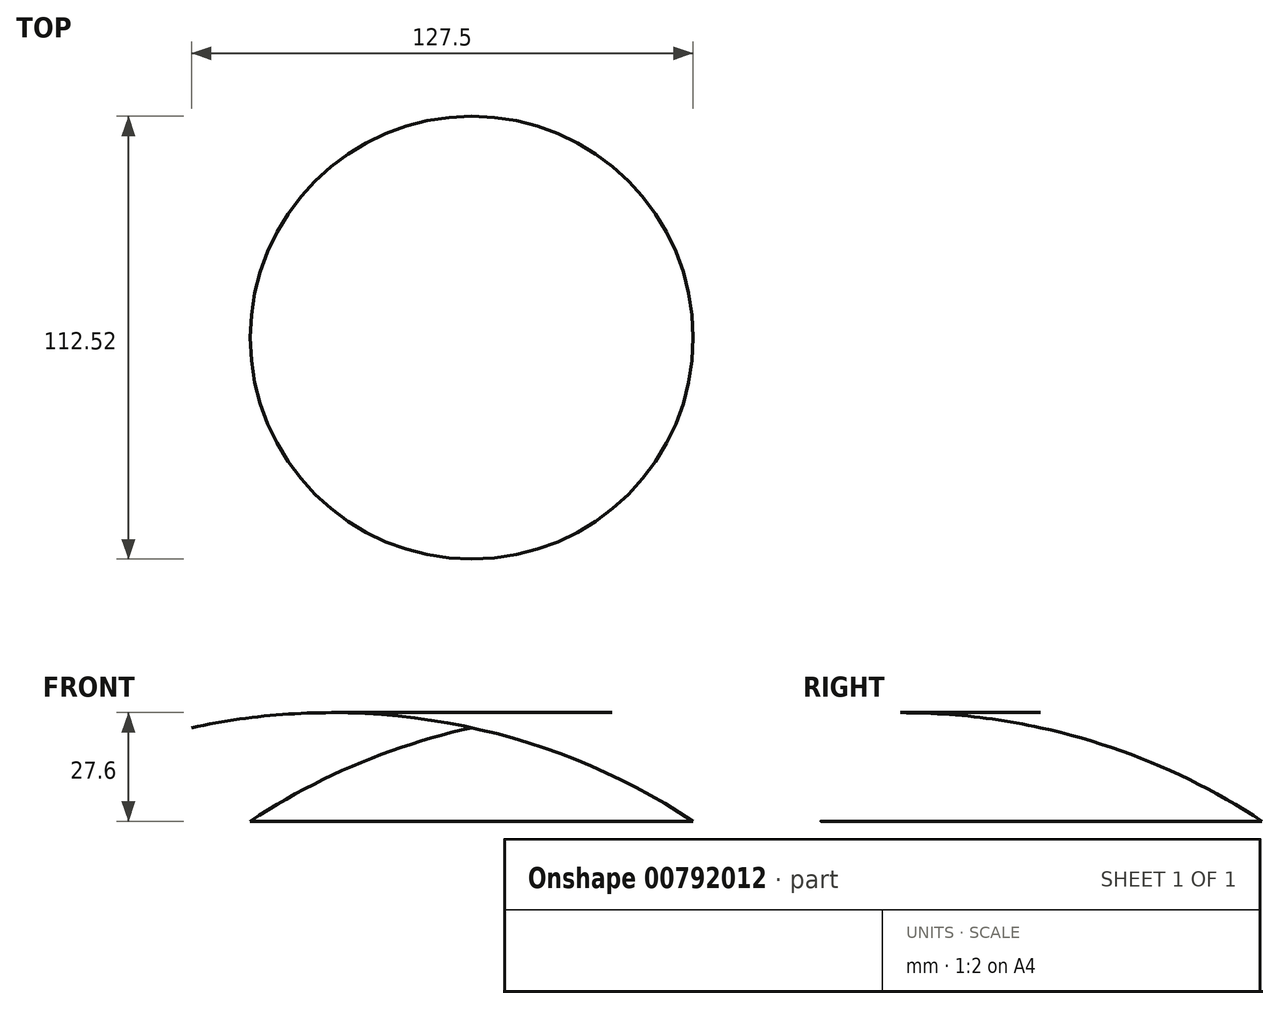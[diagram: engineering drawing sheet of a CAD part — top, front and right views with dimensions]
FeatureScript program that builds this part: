
annotation { "Feature Type Name" : "Feature", "Feature Type Description" : "" }
export const myFeature = defineFeature(function(context is Context, id is Id, definition is map)
    precondition{}
    {
        {
            var Q0;
            Q0=qCreatedBy(makeId("Front.planeOp"),FACE);
            var sketch = newSketch(context, id + "F0", { "sketchPlane" : qUnion([Q0])});
            skLineSegment(sketch, "E0", {"start": v(0, 0) * mm, "end": v(0, 23.75) * mm});
            skLineSegment(sketch, "E1", {"start": v(0, 0) * mm, "end": v(-56.26, 0) * mm});
            skArc(sketch, "E2", {"start": v(0, 23.75) * mm, "mid": v(-29.23, 14.47) * mm, "end": v(-56.26, 0) * mm});
            skSolve(sketch);
        }
        {
            var Q0;
            Q0=makeQuery(id+"F0.imprint","IMPRINT",FACE,{"disambiguationData":[TD([[makeQuery(id+"F0.imprint","IMPRINT",EDGE,{"derivedFrom":sQuery(id+"F0.wireOp",EDGE,"E0")}),1.0]])]});
            var Q1;
            Q1=sQuery(id+"F0.wireOp",EDGE,"E0");
            revolve(context, id + "F1", {"surfaceOperationType" : NewSurfaceOperationType.NEW, "entities" : qUnion([Q0]), "axis" : qUnion([Q1]), "revolveType" : RevolveType.FULL});
        }
    });
